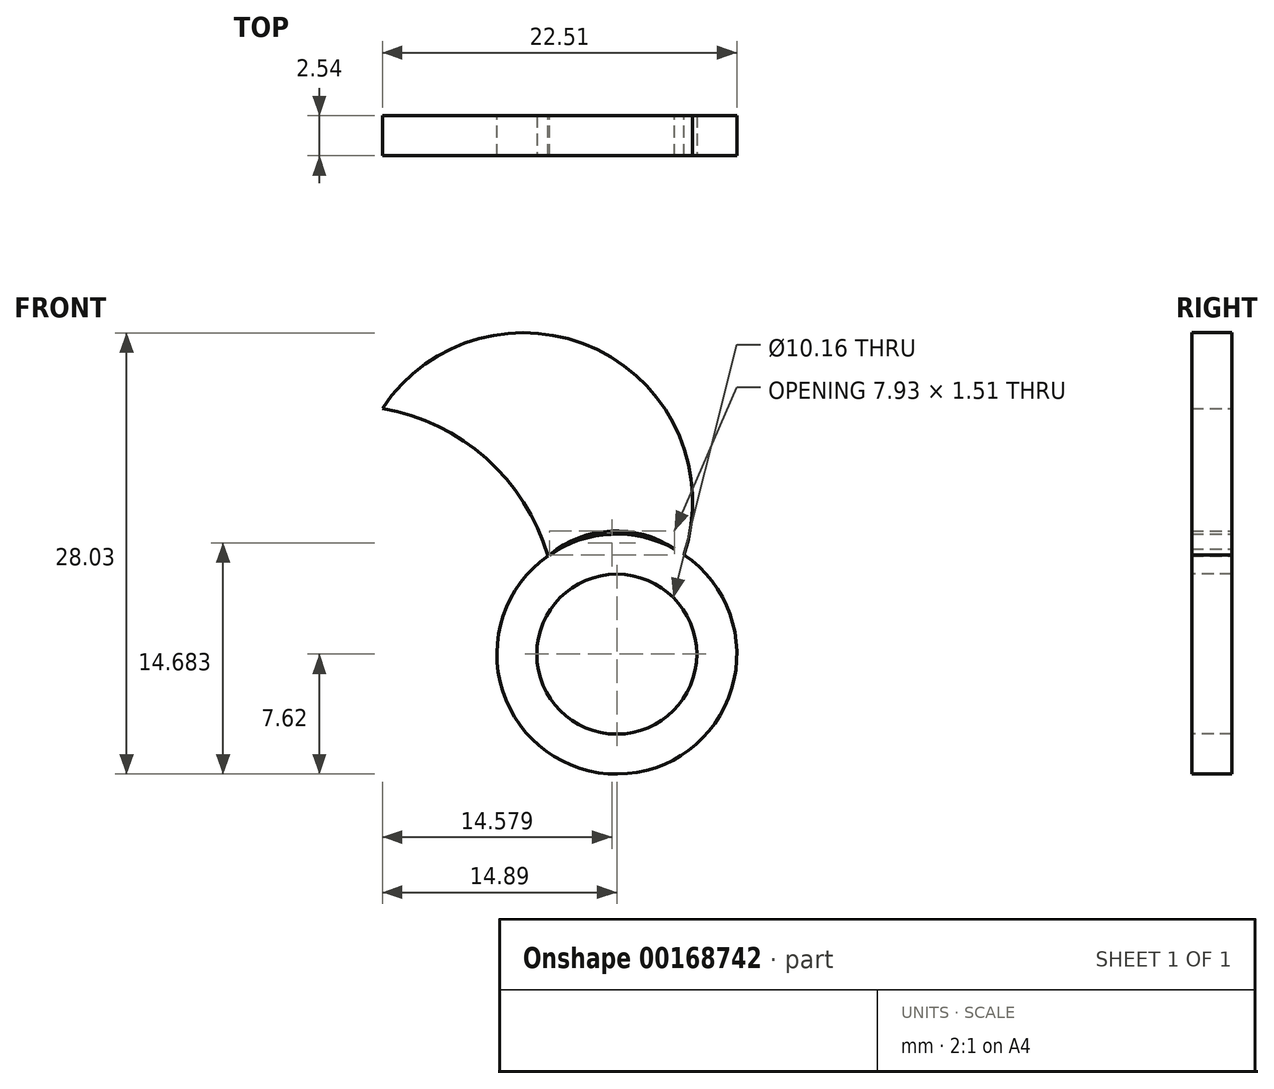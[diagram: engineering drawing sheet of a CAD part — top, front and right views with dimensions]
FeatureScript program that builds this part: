
annotation { "Feature Type Name" : "Feature", "Feature Type Description" : "" }
export const myFeature = defineFeature(function(context is Context, id is Id, definition is map)
    precondition{}
    {
        {
            var Q0;
            Q0=qCreatedBy(makeId("Front.planeOp"),FACE);
            var sketch = newSketch(context, id + "F0", { "sketchPlane" : qUnion([Q0])});
            skCircle(sketch, "E0", {"center": v(0, 0) * mm, "radius": 7.62 * mm});
            skSolve(sketch);
        }
        {
            var Q0;
            Q0 = qSketchRegion(id + "F0", true);
            extrude(context, id + "F1", {"entities" : qUnion([Q0]), "endBound" : BoundingType.SYMMETRIC, "depth" : 2.54 * mm});
        }
        {
            var Q0;
            Q0=makeQuery(id+"F1.opExtrude","CAP_FACE",FACE,{"disambiguationData":[OSD([sQuery(id+"F0.wireOp",EDGE,"E0")])],"isStart":false});
            var sketch = newSketch(context, id + "F2", { "sketchPlane" : qUnion([Q0])});
            skCircle(sketch, "E1", {"center": v(0, 0) * mm, "radius": 6.35 * mm});
            skSolve(sketch);
        }
        {
            var Q0;
            Q0=sQuery(id+"F2.wireOp",VERTEX,"E1.center");
            var Q1;
            Q1=makeQuery(id+"F1.opExtrude","SWEPT_BODY",BODY,{"disambiguationData":[OSD([sQuery(id+"F0.wireOp",EDGE,"E0")])]});
            hole(context, id + "F3", {"style" : HoleStyle.SIMPLE, "endStyle" : HoleEndStyle.THROUGH, "holeDiameter" : 10.16 * mm, "locations" : qUnion([Q0]), "scope" : qUnion([Q1]), "isTappedThrough" : true});
        }
        {
            var Q0;
            Q0=qCreatedBy(makeId("Front.planeOp"),FACE);
            var sketch = newSketch(context, id + "F4", { "sketchPlane" : qUnion([Q0])});
            skPoint(sketch, "E2", {"position": v(4.25, 6.23) * mm});
            skPoint(sketch, "E3", {"position": v(-4.37, 6.23) * mm});
            skPoint(sketch, "E4", {"position": v(-14.89, 15.61) * mm});
            skArc(sketch, "E5", {"start": v(4.25, 6.23) * mm, "mid": v(-1.2, 19.32) * mm, "end": v(-14.89, 15.61) * mm});
            skArc(sketch, "E6", {"start": v(-4.37, 6.23) * mm, "mid": v(-8.28, 12.43) * mm, "end": v(-14.89, 15.61) * mm});
            skArc(sketch, "E7", {"start": v(4.25, 6.23) * mm, "mid": v(-0.06, 7.83) * mm, "end": v(-4.37, 6.23) * mm});
            skSolve(sketch);
        }
        {
            var Q0;
            Q0=makeQuery(id+"F4.imprint","IMPRINT",FACE,{"disambiguationData":[TD([[makeQuery(id+"F4.imprint","IMPRINT",EDGE,{"derivedFrom":sQuery(id+"F4.wireOp",EDGE,"mFTq0H4n-Enze-I29F-G6DC-PtmOwYUhrqtf")}),-1.0]])]});
            var Q1;
            Q1=makeQuery(id+"F4.imprint","IMPRINT",FACE,{"disambiguationData":[TD([[makeQuery(id+"F4.imprint","IMPRINT",EDGE,{"derivedFrom":sQuery(id+"F4.wireOp",EDGE,"E5")}),1.0]])]});
            extrude(context, id + "F5", {"entities" : qUnion([Q0, Q1]), "operationType" : NewBodyOperationType.ADD, "endBound" : BoundingType.SYMMETRIC, "depth" : 2.54 * mm});
        }
    });
